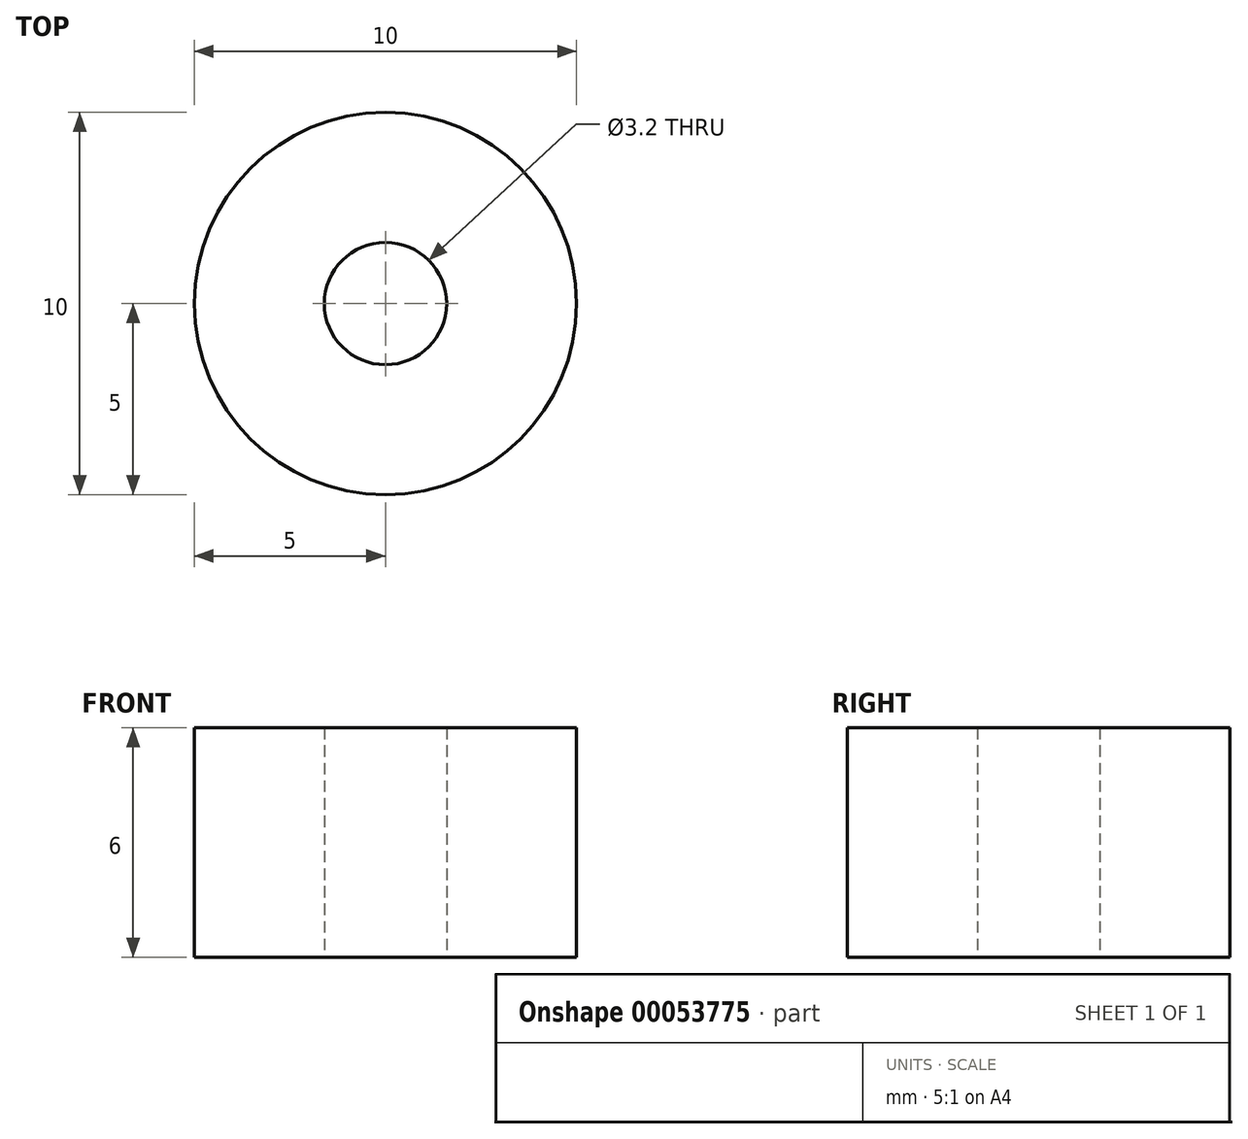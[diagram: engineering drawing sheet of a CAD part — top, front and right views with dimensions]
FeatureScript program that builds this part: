
annotation { "Feature Type Name" : "Feature", "Feature Type Description" : "" }
export const myFeature = defineFeature(function(context is Context, id is Id, definition is map)
    precondition{}
    {
        {
            var Q0;
            Q0=qCreatedBy(makeId("Top.planeOp"),FACE);
            var sketch = newSketch(context, id + "F0", { "sketchPlane" : qUnion([Q0])});
            skCircle(sketch, "E0", {"center": v(0, 0) * mm, "radius": 5 * mm});
            skCircle(sketch, "E1", {"center": v(0, 0) * mm, "radius": 1.6 * mm});
            skSolve(sketch);
        }
        {
            var Q0;
            Q0=makeQuery(id+"F0.imprint","IMPRINT",FACE,{"disambiguationData":[TD([[makeQuery(id+"F0.imprint","IMPRINT",EDGE,{"derivedFrom":sQuery(id+"F0.wireOp",EDGE,"E0")}),1.0]])]});
            extrude(context, id + "F1", {"entities" : qUnion([Q0]), "depth" : 6 * mm});
        }
    });
